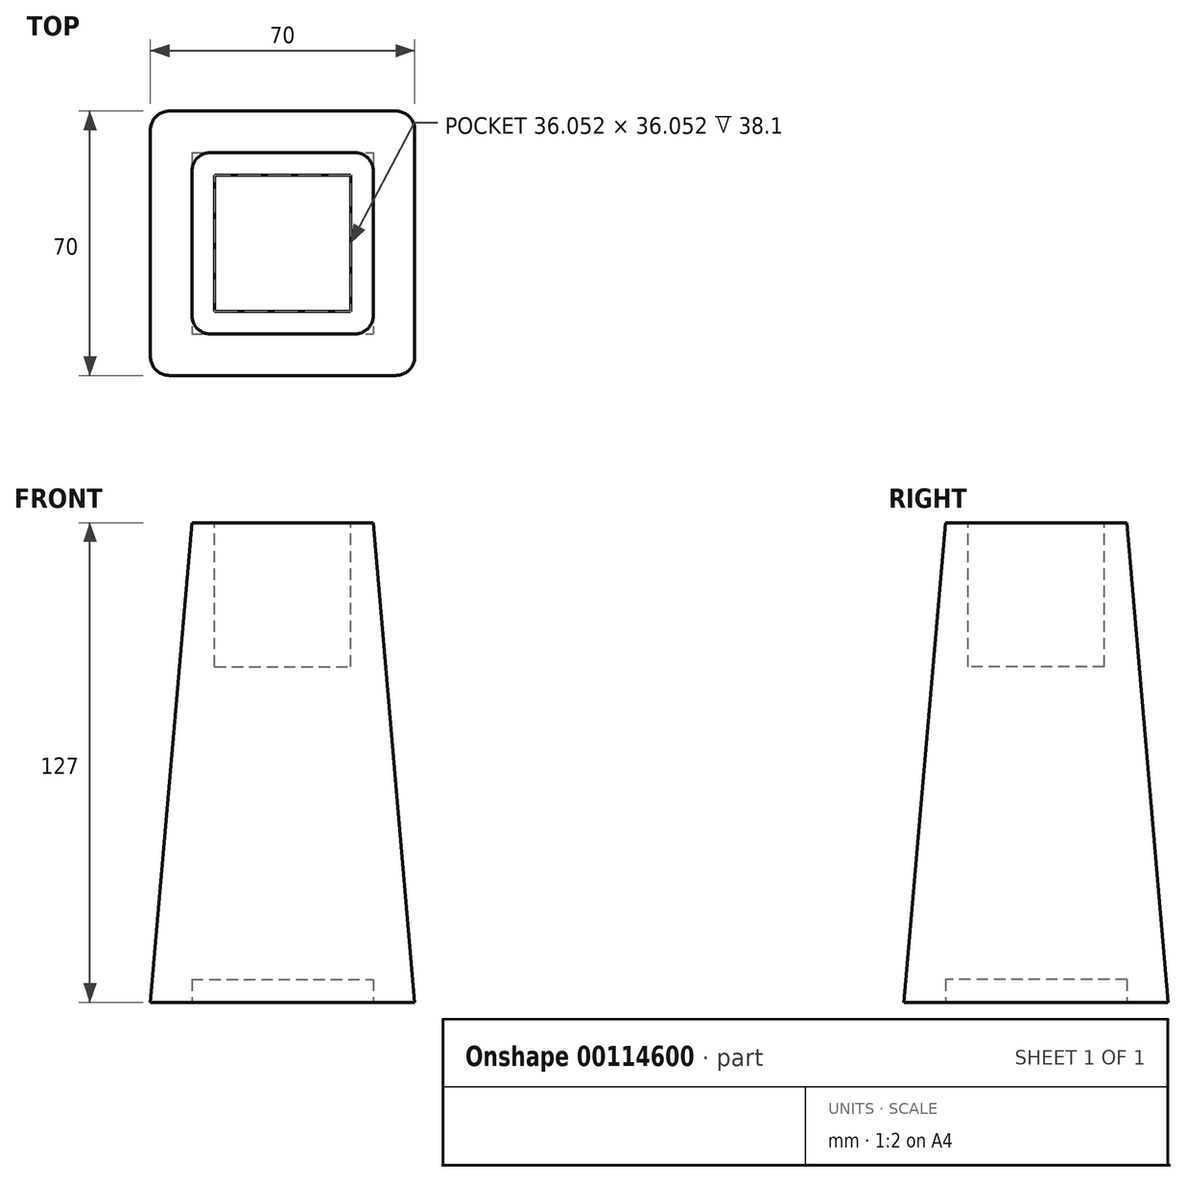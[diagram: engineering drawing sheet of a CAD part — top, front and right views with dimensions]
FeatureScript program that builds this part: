
annotation { "Feature Type Name" : "Feature", "Feature Type Description" : "" }
export const myFeature = defineFeature(function(context is Context, id is Id, definition is map)
    precondition{}
    {
        {
            var Q0;
            Q0=qCreatedBy(makeId("Top.planeOp"),FACE);
            var sketch = newSketch(context, id + "F0", { "sketchPlane" : qUnion([Q0])});
            skLineSegment(sketch, "E0.bottom", {"start": v(-18.03, 18.03) * mm, "end": v(18.03, 18.03) * mm, "construction": true});
            skLineSegment(sketch, "E0.top", {"start": v(-18.03, -18.03) * mm, "end": v(18.03, -18.03) * mm, "construction": true});
            skLineSegment(sketch, "E0.left", {"start": v(-18.03, 18.03) * mm, "end": v(-18.03, -18.03) * mm, "construction": true});
            skLineSegment(sketch, "E0.right", {"start": v(18.03, 18.03) * mm, "end": v(18.03, -18.03) * mm, "construction": true});
            skLineSegment(sketch, "E1", {"start": v(-30.77, 0) * mm, "end": v(32.73, 0) * mm, "construction": true});
            skLineSegment(sketch, "E2", {"start": v(0, 46.13) * mm, "end": v(0, -51.31) * mm, "construction": true});
            skLineSegment(sketch, "E3.bottom", {"start": v(-24.03, 24.03) * mm, "end": v(24.03, 24.03) * mm});
            skLineSegment(sketch, "E3.top", {"start": v(-24.03, -24.03) * mm, "end": v(24.03, -24.03) * mm});
            skLineSegment(sketch, "E3.left", {"start": v(-24.03, 24.03) * mm, "end": v(-24.03, -24.03) * mm});
            skLineSegment(sketch, "E3.right", {"start": v(24.03, 24.03) * mm, "end": v(24.03, -24.03) * mm});
            skSolve(sketch);
        }
        {
            var Q0;
            Q0=qCreatedBy(makeId("Top.planeOp"),FACE);
            cPlane(context, id + "F1", {"entities" : qUnion([Q0]), "cplaneType" : CPlaneType.OFFSET, "offset" : 127 * mm, "oppositeDirection" : true, "width" : 150 * mm, "height" : 150 * mm});
        }
        {
            var Q0;
            Q0=qCreatedBy(id+"F1.planeOp",FACE);
            var sketch = newSketch(context, id + "F2", { "sketchPlane" : qUnion([Q0])});
            skLineSegment(sketch, "E4.bottom", {"start": v(-35, 35) * mm, "end": v(35, 35) * mm});
            skLineSegment(sketch, "E4.top", {"start": v(-35, -35) * mm, "end": v(35, -35) * mm});
            skLineSegment(sketch, "E4.left", {"start": v(-35, 35) * mm, "end": v(-35, -35) * mm});
            skLineSegment(sketch, "E4.right", {"start": v(35, 35) * mm, "end": v(35, -35) * mm});
            skSolve(sketch);
        }
        {
            var Q0;
            Q0=makeQuery(id+"F0.imprint","IMPRINT",FACE,{"disambiguationData":[TD([[makeQuery(id+"F0.imprint","IMPRINT",EDGE,{"derivedFrom":sQuery(id+"F0.wireOp",EDGE,"E3.bottom")}),-1.0]])]});
            var Q1;
            Q1=makeQuery(id+"F2.imprint","IMPRINT",FACE,{"disambiguationData":[TD([[makeQuery(id+"F2.imprint","IMPRINT",EDGE,{"derivedFrom":sQuery(id+"F2.wireOp",EDGE,"E4.bottom")}),-1.0]])]});
            loft(context, id + "F3", {"sheetProfilesArray" : [{ "sheetProfileEntities" : qUnion([Q0]) }, { "sheetProfileEntities" : qUnion([Q1]) }]});
        }
        {
            var Q0;
            Q0=makeQuery(id+"F3.opLoft","CAP_FACE",FACE,{"disambiguationData":[OSD([makeQuery(id+"F0.imprint","IMPRINT",FACE,{"disambiguationData":[TD([[makeQuery(id+"F0.imprint","IMPRINT",EDGE,{"derivedFrom":sQuery(id+"F0.wireOp",EDGE,"E3.bottom")}),-1.0]])]})])],"isStart":true});
            var sketch = newSketch(context, id + "F4", { "sketchPlane" : qUnion([Q0])});
            skLineSegment(sketch, "E5.bottom", {"start": v(-18.03, 18.03) * mm, "end": v(18.03, 18.03) * mm});
            skLineSegment(sketch, "E5.top", {"start": v(-18.03, -18.03) * mm, "end": v(18.03, -18.03) * mm});
            skLineSegment(sketch, "E5.left", {"start": v(-18.03, 18.03) * mm, "end": v(-18.03, -18.03) * mm});
            skLineSegment(sketch, "E5.right", {"start": v(18.03, 18.03) * mm, "end": v(18.03, -18.03) * mm});
            skSolve(sketch);
        }
        {
            var Q0;
            Q0=makeQuery(id+"F4.imprint","IMPRINT",FACE,{"disambiguationData":[TD([[makeQuery(id+"F4.imprint","IMPRINT",EDGE,{"derivedFrom":sQuery(id+"F4.wireOp",EDGE,"E5.bottom")}),-1.0]])]});
            extrude(context, id + "F5", {"entities" : qUnion([Q0]), "operationType" : NewBodyOperationType.REMOVE, "oppositeDirection" : true, "depth" : 38.1 * mm});
        }
        {
            var Q0;
            Q0=makeQuery(id+"F3.opLoft","SWEPT_EDGE",EDGE,{"disambiguationData":[OSD([sQuery(id+"F0.wireOp",EDGE,"E3.top"),sQuery(id+"F0.wireOp",EDGE,"E3.left"),sQuery(id+"F2.wireOp",EDGE,"E4.top"),sQuery(id+"F2.wireOp",EDGE,"E4.left")])]});
            var Q1;
            Q1=makeQuery(id+"F3.opLoft","SWEPT_EDGE",EDGE,{"disambiguationData":[OSD([sQuery(id+"F0.wireOp",EDGE,"E3.top"),sQuery(id+"F0.wireOp",EDGE,"E3.right"),sQuery(id+"F2.wireOp",EDGE,"E4.top"),sQuery(id+"F2.wireOp",EDGE,"E4.right")])]});
            var Q2;
            Q2=makeQuery(id+"F3.opLoft","SWEPT_EDGE",EDGE,{"disambiguationData":[OSD([sQuery(id+"F0.wireOp",EDGE,"E3.bottom"),sQuery(id+"F0.wireOp",EDGE,"E3.left"),sQuery(id+"F2.wireOp",EDGE,"E4.bottom"),sQuery(id+"F2.wireOp",EDGE,"E4.left")])]});
            var Q3;
            Q3=makeQuery(id+"F3.opLoft","SWEPT_EDGE",EDGE,{"disambiguationData":[OSD([sQuery(id+"F0.wireOp",EDGE,"E3.bottom"),sQuery(id+"F0.wireOp",EDGE,"E3.right"),sQuery(id+"F2.wireOp",EDGE,"E4.bottom"),sQuery(id+"F2.wireOp",EDGE,"E4.right")])]});
            fillet(context, id + "F6", {"entities" : qUnion([Q0, Q1, Q2, Q3]), "radius" : 5 * mm, "tangentPropagation" : true, "allowEdgeOverflow" : false});
        }
        {
            var Q0;
            Q0=makeQuery(id+"F3.opLoft","CAP_FACE",FACE,{"disambiguationData":[OSD([makeQuery(id+"F2.imprint","IMPRINT",FACE,{"disambiguationData":[TD([[makeQuery(id+"F2.imprint","IMPRINT",EDGE,{"derivedFrom":sQuery(id+"F2.wireOp",EDGE,"E4.bottom")}),-1.0]])]})])],"isStart":true});
            var sketch = newSketch(context, id + "F7", { "sketchPlane" : qUnion([Q0])});
            skLineSegment(sketch, "E6.0", {"start": v(24.03, -24.03) * mm, "end": v(24.03, 24.03) * mm});
            skLineSegment(sketch, "E6.1", {"start": v(-24.03, 24.03) * mm, "end": v(24.03, 24.03) * mm});
            skLineSegment(sketch, "E6.2", {"start": v(-24.03, -24.03) * mm, "end": v(-24.03, 24.03) * mm});
            skLineSegment(sketch, "E6.3", {"start": v(-24.03, -24.03) * mm, "end": v(24.03, -24.03) * mm});
            skSolve(sketch);
        }
        {
            var Q0;
            Q0 = qSketchRegion(id + "F7", true);
            extrude(context, id + "F8", {"entities" : qUnion([Q0]), "operationType" : NewBodyOperationType.REMOVE, "oppositeDirection" : true, "depth" : 6 * mm});
        }
    });
